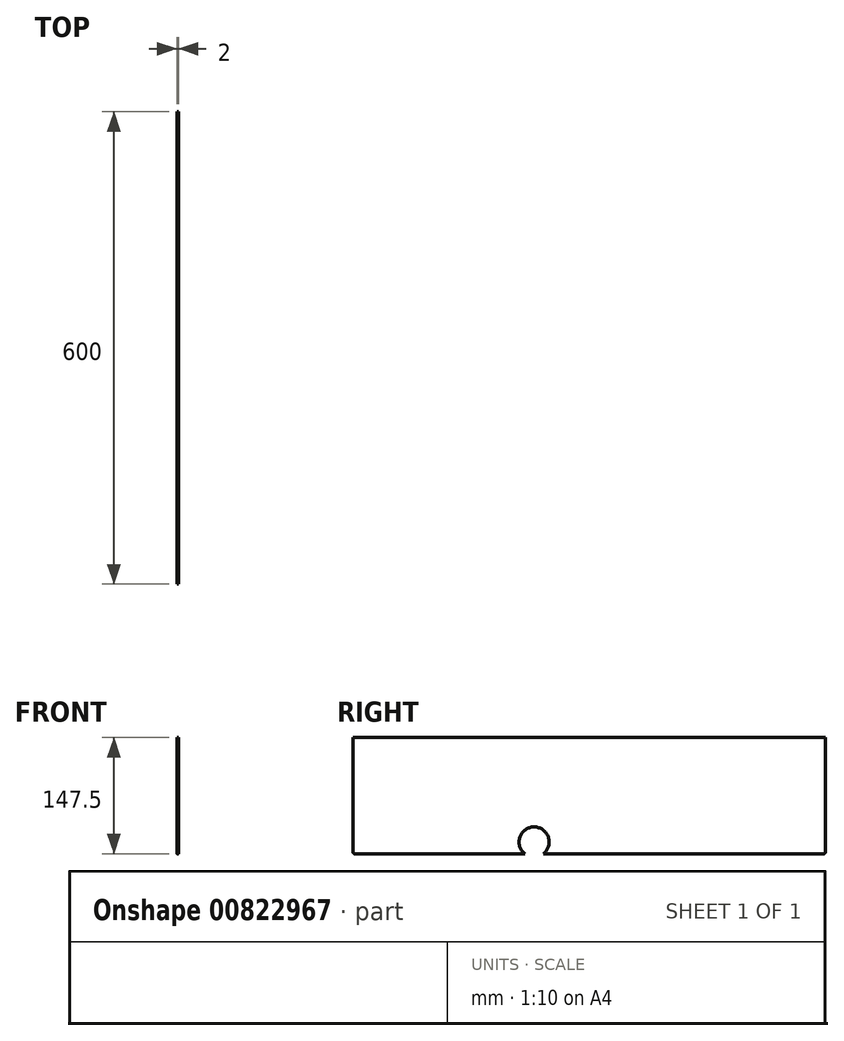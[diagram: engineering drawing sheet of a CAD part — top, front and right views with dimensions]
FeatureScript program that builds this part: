
annotation { "Feature Type Name" : "Feature", "Feature Type Description" : "" }
export const myFeature = defineFeature(function(context is Context, id is Id, definition is map)
    precondition{}
    {
        {
            var Q0;
            Q0=qCreatedBy(makeId("Right.planeOp"),FACE);
            var sketch = newSketch(context, id + "F0", { "sketchPlane" : qUnion([Q0])});
            skLineSegment(sketch, "E0.bottom", {"start": v(-300, -73.75) * mm, "end": v(300, -73.75) * mm});
            skLineSegment(sketch, "E0.top", {"start": v(-300, 73.75) * mm, "end": v(300, 73.75) * mm});
            skLineSegment(sketch, "E0.left", {"start": v(-300, -73.75) * mm, "end": v(-300, 73.75) * mm});
            skLineSegment(sketch, "E0.right", {"start": v(300, -73.75) * mm, "end": v(300, 73.75) * mm});
            skPoint(sketch, "E0.middle", {"position": v(0, 0) * mm});
            skSolve(sketch);
        }
        {
            var Q0;
            Q0=qSketchRegion(id+"F0",true);
            extrude(context, id + "F1", {"entities" : qUnion([Q0]), "depth" : 2 * mm, "offsetDistance" : 25 * mm});
        }
        {
            var Q0;
            Q0=makeQuery(id+"F1.opExtrude","SWEPT_EDGE",EDGE,{"disambiguationData":[OSD([sQuery(id+"F0.wireOp",EDGE,"E0.bottom"),sQuery(id+"F0.wireOp",EDGE,"E0.left")])]});
            var Q1;
            Q1=makeQuery(id+"F1.opExtrude","SWEPT_EDGE",EDGE,{"disambiguationData":[OSD([sQuery(id+"F0.wireOp",EDGE,"E0.bottom"),sQuery(id+"F0.wireOp",EDGE,"E0.right")])]});
            fillet(context, id + "F2", {"entities" : qUnion([Q0, Q1]), "radius" : 2 * mm, "tangentPropagation" : true, "allowEdgeOverflow" : false});
        }
        {
            var Q0;
            Q0=makeQuery(id+"F1.opExtrude","CAP_FACE",FACE,{"disambiguationData":[OSD([sQuery(id+"F0.wireOp",EDGE,"E0.bottom"),sQuery(id+"F0.wireOp",EDGE,"E0.top"),sQuery(id+"F0.wireOp",EDGE,"E0.left"),sQuery(id+"F0.wireOp",EDGE,"E0.right")])],"isStart":false});
            var sketch = newSketch(context, id + "F3", { "sketchPlane" : qUnion([Q0])});
            skLineSegment(sketch, "E1.0", {"start": v(-300, -71.75) * mm, "end": v(-300, 73.75) * mm, "construction": true});
            skLineSegment(sketch, "E2.0", {"start": v(-298, -73.75) * mm, "end": v(298, -73.75) * mm, "construction": true});
            skCircle(sketch, "E3", {"center": v(-70, -58.75) * mm, "radius": 19.05 * mm});
            skSolve(sketch);
        }
        {
            var Q0;
            Q0 = qSketchRegion(id + "F3", true);
            extrude(context, id + "F4", {"entities" : qUnion([Q0]), "operationType" : NewBodyOperationType.REMOVE, "oppositeDirection" : true, "depth" : 25 * mm, "offsetDistance" : 25 * mm});
        }
    });
